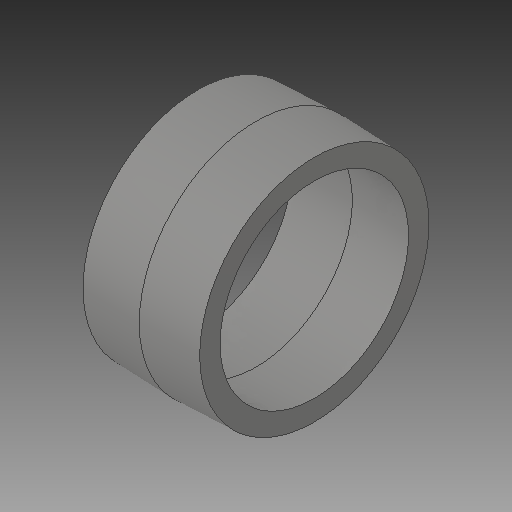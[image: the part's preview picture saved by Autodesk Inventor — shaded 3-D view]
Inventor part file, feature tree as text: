
AUTODESK INVENTOR PART (.ipt)
format: ipt  version: 2017 (Build 210142000, 142)  size: 117,760 bytes
history: native  units: in
note: dims shown in document units (in); Inventor stores cm internally (conversion verified against a paired STEP export)
features: revolve x1
ambient origin geometry x8: Origin, YZ Plane, XZ Plane, XY Plane, X Axis, Y Axis, Z Axis, Center Point
bodies: Solid1 (feature_tree)
feature tree (1):
  revolve  "Revolve1"  [1 undecoded]
note: 1 required parameter value undecoded (feature->parameter linkage not recoverable at this tier; creation-order binding heuristic only, values carry confidence <= 0.55)
